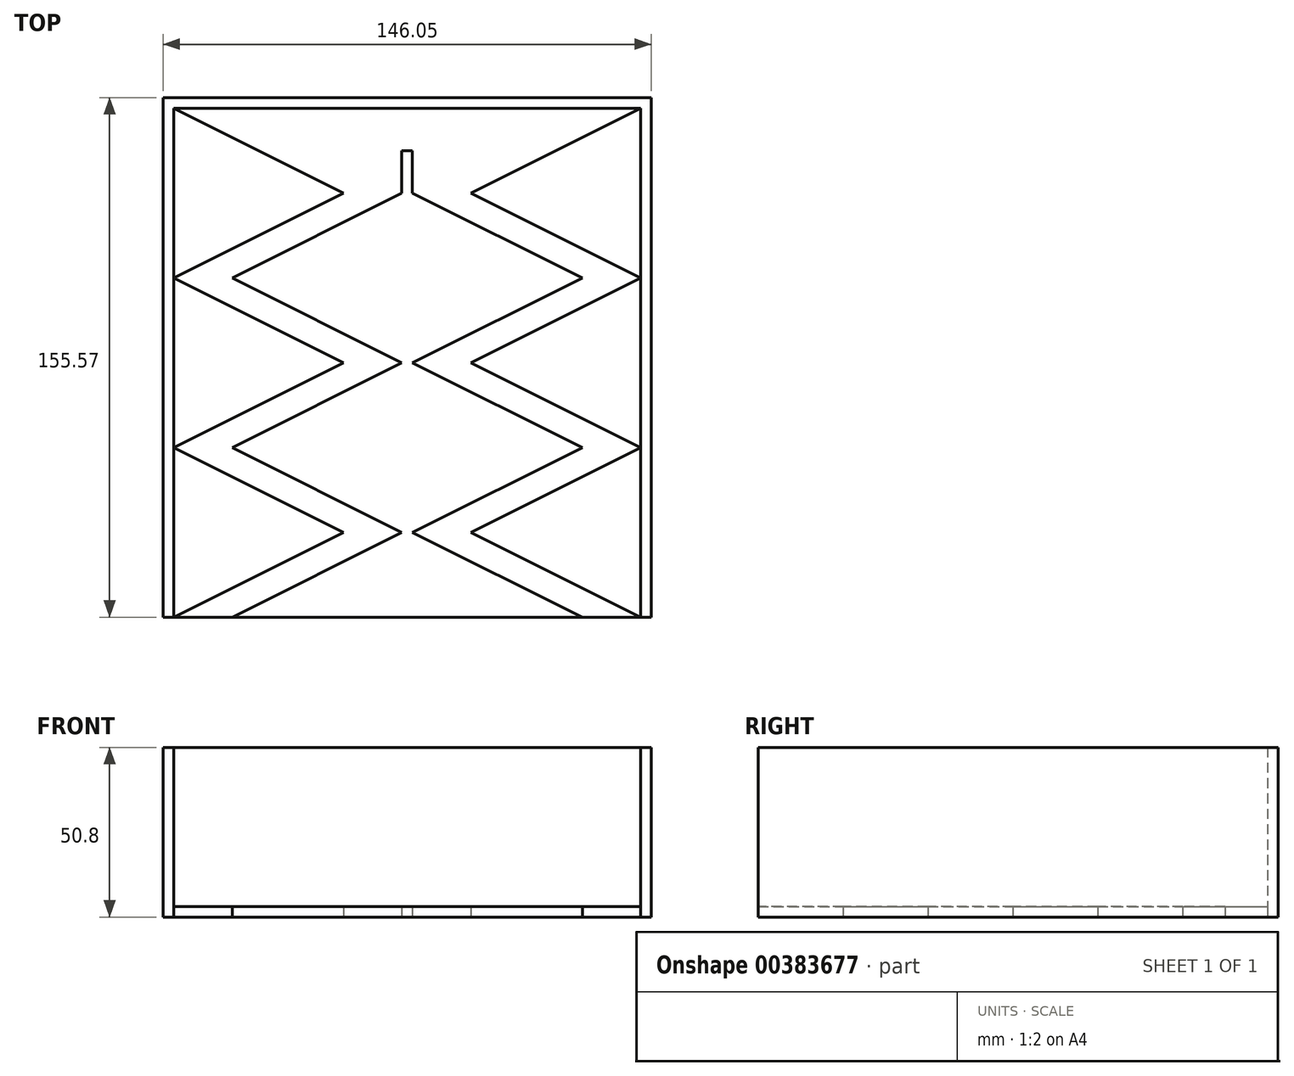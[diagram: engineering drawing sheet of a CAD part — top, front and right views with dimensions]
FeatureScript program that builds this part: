
annotation { "Feature Type Name" : "Feature", "Feature Type Description" : "" }
export const myFeature = defineFeature(function(context is Context, id is Id, definition is map)
    precondition{}
    {
        {
            var Q0;
            Q0=qCreatedBy(makeId("Top.planeOp"),FACE);
            var sketch = newSketch(context, id + "F0", { "sketchPlane" : qUnion([Q0])});
            skLineSegment(sketch, "E0.bottom", {"start": v(0, 0) * mm, "end": v(146.05, 0) * mm});
            skLineSegment(sketch, "E0.top", {"start": v(0, 155.57) * mm, "end": v(146.05, 155.57) * mm});
            skLineSegment(sketch, "E0.left", {"start": v(0, 0) * mm, "end": v(0, 155.57) * mm});
            skLineSegment(sketch, "E0.right", {"start": v(146.05, 0) * mm, "end": v(146.05, 155.57) * mm});
            skLineSegment(sketch, "E1", {"start": v(3.18, 0) * mm, "end": v(53.97, 25.4) * mm});
            skLineSegment(sketch, "E2", {"start": v(53.97, 25.4) * mm, "end": v(3.17, 50.8) * mm});
            skLineSegment(sketch, "E3", {"start": v(3.17, 50.8) * mm, "end": v(53.97, 76.2) * mm});
            skLineSegment(sketch, "E4", {"start": v(53.97, 76.2) * mm, "end": v(3.17, 101.6) * mm});
            skLineSegment(sketch, "E5", {"start": v(3.17, 101.6) * mm, "end": v(53.97, 127) * mm});
            skLineSegment(sketch, "E6", {"start": v(53.97, 127) * mm, "end": v(3.17, 152.4) * mm});
            skLineSegment(sketch, "E7.bottom", {"start": v(3.17, 0) * mm, "end": v(142.88, 0) * mm});
            skLineSegment(sketch, "E7.top", {"start": v(3.17, 152.4) * mm, "end": v(142.87, 152.4) * mm});
            skLineSegment(sketch, "E7.left", {"start": v(3.17, 0) * mm, "end": v(3.17, 152.4) * mm});
            skLineSegment(sketch, "E7.right", {"start": v(142.88, 0) * mm, "end": v(142.88, 152.4) * mm});
            skLineSegment(sketch, "E8", {"start": v(20.64, 0) * mm, "end": v(71.44, 25.4) * mm});
            skLineSegment(sketch, "E9", {"start": v(71.44, 25.4) * mm, "end": v(20.64, 50.8) * mm});
            skLineSegment(sketch, "E10", {"start": v(20.64, 50.8) * mm, "end": v(71.44, 76.2) * mm});
            skLineSegment(sketch, "E11", {"start": v(71.44, 76.2) * mm, "end": v(20.64, 101.6) * mm});
            skLineSegment(sketch, "E12", {"start": v(20.64, 101.6) * mm, "end": v(71.44, 127) * mm});
            skLineSegment(sketch, "E13", {"start": v(71.44, 127) * mm, "end": v(71.44, 139.7) * mm});
            skLineSegment(sketch, "E14", {"start": v(71.44, 139.7) * mm, "end": v(74.61, 139.7) * mm});
            skLineSegment(sketch, "E15", {"start": v(74.61, 139.7) * mm, "end": v(74.61, 127) * mm});
            skLineSegment(sketch, "E16", {"start": v(74.61, 127) * mm, "end": v(125.41, 101.6) * mm});
            skLineSegment(sketch, "E17", {"start": v(125.41, 101.6) * mm, "end": v(74.61, 76.2) * mm});
            skLineSegment(sketch, "E18", {"start": v(74.61, 76.2) * mm, "end": v(125.41, 50.8) * mm});
            skLineSegment(sketch, "E19", {"start": v(125.41, 50.8) * mm, "end": v(74.61, 25.4) * mm});
            skLineSegment(sketch, "E20", {"start": v(74.61, 25.4) * mm, "end": v(125.41, 0) * mm});
            skLineSegment(sketch, "E21", {"start": v(142.88, 0) * mm, "end": v(92.07, 25.4) * mm});
            skLineSegment(sketch, "E22", {"start": v(92.07, 25.4) * mm, "end": v(142.87, 50.8) * mm});
            skLineSegment(sketch, "E23", {"start": v(142.87, 50.8) * mm, "end": v(92.07, 76.2) * mm});
            skLineSegment(sketch, "E24", {"start": v(92.07, 76.2) * mm, "end": v(142.87, 101.6) * mm});
            skLineSegment(sketch, "E25", {"start": v(142.87, 101.6) * mm, "end": v(92.07, 127) * mm});
            skLineSegment(sketch, "E26", {"start": v(92.07, 127) * mm, "end": v(142.88, 152.4) * mm});
            skSolve(sketch);
        }
        {
            var Q0;
            {var subQ0=sQuery(id+"F0.wireOp",EDGE,"E1");Q0=makeQuery(id+"F0.imprint","IMPRINT",FACE,{"disambiguationData":[TD([[makeQuery(id+"F0.imprint","IMPRINT",EDGE,{"derivedFrom":subQ0}),-1.0]])]});}
            var Q1;
            {var subQ2=sQuery(id+"F0.wireOp",EDGE,"E25");Q1=makeQuery(id+"F0.imprint","IMPRINT",FACE,{"disambiguationData":[TD([[makeQuery(id+"F0.imprint","IMPRINT",EDGE,{"derivedFrom":subQ2}),-1.0]])]});}
            var Q2;
            Q2=makeQuery(id+"F0.imprint","IMPRINT",FACE,{"disambiguationData":[TD([[makeQuery(id+"F0.imprint","IMPRINT",EDGE,{"derivedFrom":sQuery(id+"F0.wireOp",EDGE,"E0.top")}),-1.0]])]});
            var Q3;
            {var subQ0=sQuery(id+"F0.wireOp",EDGE,"E23");Q3=makeQuery(id+"F0.imprint","IMPRINT",FACE,{"disambiguationData":[TD([[makeQuery(id+"F0.imprint","IMPRINT",EDGE,{"derivedFrom":subQ0}),-1.0]])]});}
            var Q4;
            {var subQ0=sQuery(id+"F0.wireOp",EDGE,"E21");Q4=makeQuery(id+"F0.imprint","IMPRINT",FACE,{"disambiguationData":[TD([[makeQuery(id+"F0.imprint","IMPRINT",EDGE,{"derivedFrom":subQ0}),-1.0]])]});}
            var Q5;
            {var subQ0=sQuery(id+"F0.wireOp",EDGE,"E8");Q5=makeQuery(id+"F0.imprint","IMPRINT",FACE,{"disambiguationData":[TD([[makeQuery(id+"F0.imprint","IMPRINT",EDGE,{"derivedFrom":subQ0}),-1.0]])]});}
            var Q6;
            {var subQ0=sQuery(id+"F0.wireOp",EDGE,"E1");Q6=makeQuery(id+"F0.imprint","IMPRINT",FACE,{"disambiguationData":[TD([[makeQuery(id+"F0.imprint","IMPRINT",EDGE,{"derivedFrom":subQ0}),1.0]])]});}
            var Q7;
            {var subQ0=sQuery(id+"F0.wireOp",EDGE,"E3");Q7=makeQuery(id+"F0.imprint","IMPRINT",FACE,{"disambiguationData":[TD([[makeQuery(id+"F0.imprint","IMPRINT",EDGE,{"derivedFrom":subQ0}),1.0]])]});}
            var Q8;
            {var subQ0=sQuery(id+"F0.wireOp",EDGE,"E5");Q8=makeQuery(id+"F0.imprint","IMPRINT",FACE,{"disambiguationData":[TD([[makeQuery(id+"F0.imprint","IMPRINT",EDGE,{"derivedFrom":subQ0}),1.0]])]});}
            extrude(context, id + "F1", {"entities" : qUnion([Q0, Q1, Q2, Q3, Q4, Q5, Q6, Q7, Q8]), "oppositeDirection" : true, "depth" : 1 / 203.2 * mm});
        }
        {
            var Q0;
            Q0=makeQuery(id+"F0.imprint","IMPRINT",FACE,{"disambiguationData":[TD([[makeQuery(id+"F0.imprint","IMPRINT",EDGE,{"derivedFrom":sQuery(id+"F0.wireOp",EDGE,"E0.top")}),-1.0]])]});
            extrude(context, id + "F2", {"entities" : qUnion([Q0]), "operationType" : NewBodyOperationType.ADD, "depth" : 50.8 * mm});
        }
        {
            var Q0;
            {var subQ0=sQuery(id+"F0.wireOp",EDGE,"E5");Q0=makeQuery(id+"F0.imprint","IMPRINT",FACE,{"disambiguationData":[TD([[makeQuery(id+"F0.imprint","IMPRINT",EDGE,{"derivedFrom":subQ0}),1.0]])]});}
            var Q1;
            {var subQ0=sQuery(id+"F0.wireOp",EDGE,"E3");Q1=makeQuery(id+"F0.imprint","IMPRINT",FACE,{"disambiguationData":[TD([[makeQuery(id+"F0.imprint","IMPRINT",EDGE,{"derivedFrom":subQ0}),1.0]])]});}
            var Q2;
            {var subQ0=sQuery(id+"F0.wireOp",EDGE,"E1");Q2=makeQuery(id+"F0.imprint","IMPRINT",FACE,{"disambiguationData":[TD([[makeQuery(id+"F0.imprint","IMPRINT",EDGE,{"derivedFrom":subQ0}),1.0]])]});}
            var Q3;
            {var subQ0=sQuery(id+"F0.wireOp",EDGE,"E21");Q3=makeQuery(id+"F0.imprint","IMPRINT",FACE,{"disambiguationData":[TD([[makeQuery(id+"F0.imprint","IMPRINT",EDGE,{"derivedFrom":subQ0}),-1.0]])]});}
            var Q4;
            {var subQ0=sQuery(id+"F0.wireOp",EDGE,"E23");Q4=makeQuery(id+"F0.imprint","IMPRINT",FACE,{"disambiguationData":[TD([[makeQuery(id+"F0.imprint","IMPRINT",EDGE,{"derivedFrom":subQ0}),-1.0]])]});}
            var Q5;
            {var subQ2=sQuery(id+"F0.wireOp",EDGE,"E25");Q5=makeQuery(id+"F0.imprint","IMPRINT",FACE,{"disambiguationData":[TD([[makeQuery(id+"F0.imprint","IMPRINT",EDGE,{"derivedFrom":subQ2}),-1.0]])]});}
            var Q6;
            {var subQ0=sQuery(id+"F0.wireOp",EDGE,"E8");Q6=makeQuery(id+"F0.imprint","IMPRINT",FACE,{"disambiguationData":[TD([[makeQuery(id+"F0.imprint","IMPRINT",EDGE,{"derivedFrom":subQ0}),-1.0]])]});}
            extrude(context, id + "F3", {"entities" : qUnion([Q0, Q1, Q2, Q3, Q4, Q5, Q6]), "operationType" : NewBodyOperationType.ADD, "depth" : 3.17 * mm});
        }
    });
